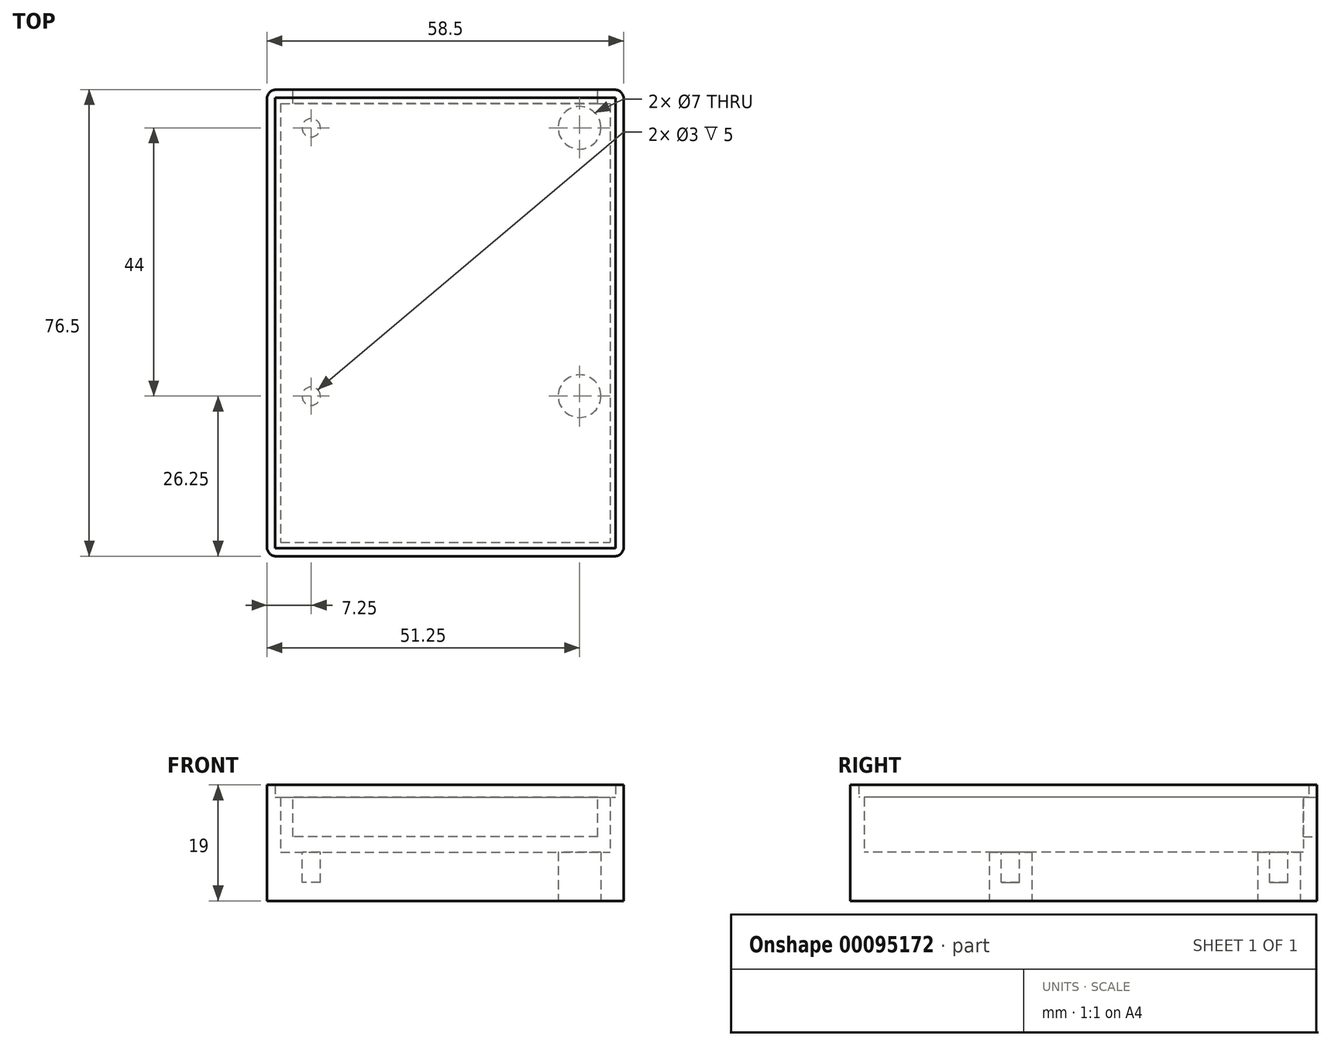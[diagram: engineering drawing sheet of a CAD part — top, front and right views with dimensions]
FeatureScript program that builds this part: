
annotation { "Feature Type Name" : "Feature", "Feature Type Description" : "" }
export const myFeature = defineFeature(function(context is Context, id is Id, definition is map)
    precondition{}
    {
        {
            var Q0;
            Q0=qCreatedBy(makeId("Top.planeOp"),FACE);
            var sketch = newSketch(context, id + "F0", { "sketchPlane" : qUnion([Q0])});
            skLineSegment(sketch, "E0.bottom", {"start": v(-25, 34) * mm, "end": v(25, 34) * mm, "construction": true});
            skLineSegment(sketch, "E0.top", {"start": v(-25, -34) * mm, "end": v(25, -34) * mm, "construction": true});
            skLineSegment(sketch, "E0.left", {"start": v(-25, 34) * mm, "end": v(-25, -34) * mm, "construction": true});
            skLineSegment(sketch, "E0.right", {"start": v(25, 34) * mm, "end": v(25, -34) * mm, "construction": true});
            skPoint(sketch, "E0.middle", {"position": v(0, 0) * mm});
            skCircle(sketch, "E1", {"center": v(-22, 32) * mm, "radius": 0.75 * mm, "construction": true});
            skCircle(sketch, "E2", {"center": v(-22, -12) * mm, "radius": 0.75 * mm, "construction": true});
            skLineSegment(sketch, "E3", {"start": v(0, 34) * mm, "end": v(0, -34) * mm, "construction": true});
            skCircle(sketch, "E4.MirrorC", {"center": v(22, 32) * mm, "radius": 0.75 * mm, "construction": true});
            skCircle(sketch, "E5.MirrorC", {"center": v(22, -12) * mm, "radius": 0.75 * mm, "construction": true});
            skLineSegment(sketch, "E6.0", {"start": v(-27, 36) * mm, "end": v(-27, -36) * mm});
            skLineSegment(sketch, "E6.1", {"start": v(-27, 36) * mm, "end": v(27, 36) * mm});
            skLineSegment(sketch, "E6.2", {"start": v(27, 36) * mm, "end": v(27, -36) * mm});
            skLineSegment(sketch, "E6.3", {"start": v(-27, -36) * mm, "end": v(27, -36) * mm});
            skLineSegment(sketch, "E7.0", {"start": v(-29.25, 38.25) * mm, "end": v(-29.25, -38.25) * mm});
            skLineSegment(sketch, "E7.1", {"start": v(-29.25, 38.25) * mm, "end": v(29.25, 38.25) * mm});
            skLineSegment(sketch, "E7.2", {"start": v(29.25, 38.25) * mm, "end": v(29.25, -38.25) * mm});
            skLineSegment(sketch, "E7.3", {"start": v(-29.25, -38.25) * mm, "end": v(29.25, -38.25) * mm});
            skCircle(sketch, "E8", {"center": v(-22, 32) * mm, "radius": 3.5 * mm});
            skCircle(sketch, "E9", {"center": v(-22, -12) * mm, "radius": 3.5 * mm});
            skCircle(sketch, "E10.MirrorC", {"center": v(22, 32) * mm, "radius": 3.5 * mm});
            skCircle(sketch, "E11.MirrorC", {"center": v(22, -12) * mm, "radius": 3.5 * mm});
            skSolve(sketch);
        }
        {
            var Q0;
            Q0=qSketchRegion(id+"F0",true);
            var Q1;
            Q1=makeQuery(id+"F0.imprint","IMPRINT",FACE,{"disambiguationData":[TD([[makeQuery(id+"F0.imprint","IMPRINT",EDGE,{"derivedFrom":sQuery(id+"F0.wireOp",EDGE,"E6.0")}),1.0]])]});
            var Q2;
            Q2=makeQuery(id+"F0.imprint","IMPRINT",FACE,{"disambiguationData":[TD([[makeQuery(id+"F0.imprint","IMPRINT",EDGE,{"derivedFrom":sQuery(id+"F0.wireOp",EDGE,"E8")}),1.0]])]});
            var Q3;
            Q3=makeQuery(id+"F0.imprint","IMPRINT",FACE,{"disambiguationData":[TD([[makeQuery(id+"F0.imprint","IMPRINT",EDGE,{"derivedFrom":sQuery(id+"F0.wireOp",EDGE,"E10.MirrorC")}),-1.0]])]});
            var Q4;
            Q4=makeQuery(id+"F0.imprint","IMPRINT",FACE,{"disambiguationData":[TD([[makeQuery(id+"F0.imprint","IMPRINT",EDGE,{"derivedFrom":sQuery(id+"F0.wireOp",EDGE,"E11.MirrorC")}),-1.0]])]});
            var Q5;
            Q5=makeQuery(id+"F0.imprint","IMPRINT",FACE,{"disambiguationData":[TD([[makeQuery(id+"F0.imprint","IMPRINT",EDGE,{"derivedFrom":sQuery(id+"F0.wireOp",EDGE,"E9")}),1.0]])]});
            extrude(context, id + "F1", {"entities" : qUnion([Q0, Q1, Q2, Q3, Q4, Q5]), "depth" : 1 * mm});
        }
        {
            var Q0;
            Q0=makeQuery(id+"F0.imprint","IMPRINT",FACE,{"disambiguationData":[TD([[makeQuery(id+"F0.imprint","IMPRINT",EDGE,{"derivedFrom":sQuery(id+"F0.wireOp",EDGE,"E6.0")}),-1.0]])]});
            extrude(context, id + "F2", {"entities" : qUnion([Q0]), "operationType" : NewBodyOperationType.ADD, "depth" : 19 * mm});
        }
        {
            var Q0;
            Q0=makeQuery(id+"F0.imprint","IMPRINT",FACE,{"disambiguationData":[TD([[makeQuery(id+"F0.imprint","IMPRINT",EDGE,{"derivedFrom":sQuery(id+"F0.wireOp",EDGE,"E9")}),1.0]])]});
            var Q1;
            Q1=makeQuery(id+"F0.imprint","IMPRINT",FACE,{"disambiguationData":[TD([[makeQuery(id+"F0.imprint","IMPRINT",EDGE,{"derivedFrom":sQuery(id+"F0.wireOp",EDGE,"E11.MirrorC")}),-1.0]])]});
            var Q2;
            Q2=makeQuery(id+"F0.imprint","IMPRINT",FACE,{"disambiguationData":[TD([[makeQuery(id+"F0.imprint","IMPRINT",EDGE,{"derivedFrom":sQuery(id+"F0.wireOp",EDGE,"E8")}),1.0]])]});
            var Q3;
            Q3=makeQuery(id+"F0.imprint","IMPRINT",FACE,{"disambiguationData":[TD([[makeQuery(id+"F0.imprint","IMPRINT",EDGE,{"derivedFrom":sQuery(id+"F0.wireOp",EDGE,"E10.MirrorC")}),-1.0]])]});
            extrude(context, id + "F3", {"entities" : qUnion([Q0, Q1, Q2, Q3]), "operationType" : NewBodyOperationType.ADD, "depth" : 8 * mm});
        }
        {
            var Q0;
            Q0=makeQuery(id+"F3.opExtrude","CAP_FACE",FACE,{"disambiguationData":[OSD([sQuery(id+"F0.wireOp",EDGE,"E11.MirrorC")])],"isStart":false});
            var sketch = newSketch(context, id + "F4", { "sketchPlane" : qUnion([Q0])});
            skCircle(sketch, "E12", {"center": v(22, -12) * mm, "radius": 1.5 * mm});
            skCircle(sketch, "E13", {"center": v(22, 32) * mm, "radius": 1.5 * mm});
            skLineSegment(sketch, "E14", {"start": v(0, -31.84) * mm, "end": v(0, 27.8) * mm, "construction": true});
            skCircle(sketch, "E15.MirrorC", {"center": v(-22, -12) * mm, "radius": 1.5 * mm});
            skCircle(sketch, "E16.MirrorC", {"center": v(-22, 32) * mm, "radius": 1.5 * mm});
            skSolve(sketch);
        }
        {
            var Q0;
            Q0=qSketchRegion(id+"F4",true);
            extrude(context, id + "F5", {"entities" : qUnion([Q0]), "operationType" : NewBodyOperationType.REMOVE, "oppositeDirection" : true, "depth" : 5 * mm});
        }
        {
            var Q0;
            Q0=makeQuery(id+"F2.opExtrude","CAP_FACE",FACE,{"disambiguationData":[OSD([sQuery(id+"F0.wireOp",EDGE,"E6.0"),sQuery(id+"F0.wireOp",EDGE,"E6.1"),sQuery(id+"F0.wireOp",EDGE,"E6.2"),sQuery(id+"F0.wireOp",EDGE,"E6.3"),sQuery(id+"F0.wireOp",EDGE,"E7.0"),sQuery(id+"F0.wireOp",EDGE,"E7.1"),sQuery(id+"F0.wireOp",EDGE,"E7.2"),sQuery(id+"F0.wireOp",EDGE,"E7.3")])],"isStart":false});
            var sketch = newSketch(context, id + "F6", { "sketchPlane" : qUnion([Q0])});
            skLineSegment(sketch, "E17.0", {"start": v(27.9, 36.9) * mm, "end": v(27.9, -36.9) * mm});
            skLineSegment(sketch, "E17.1", {"start": v(-27.9, 36.9) * mm, "end": v(27.9, 36.9) * mm});
            skLineSegment(sketch, "E17.2", {"start": v(-27.9, 36.9) * mm, "end": v(-27.9, -36.9) * mm});
            skLineSegment(sketch, "E17.3", {"start": v(-27.9, -36.9) * mm, "end": v(27.9, -36.9) * mm});
            skSolve(sketch);
        }
        {
            var Q0;
            Q0=qSketchRegion(id+"F6",true);
            extrude(context, id + "F7", {"entities" : qUnion([Q0]), "operationType" : NewBodyOperationType.REMOVE, "oppositeDirection" : true, "depth" : 2 * mm});
        }
        {
            var Q0;
            {var subQ0=sQuery(id+"F0.wireOp",EDGE,"E7.1");Q0=makeQuery(id+"F2.boolean.opBoolean","MERGE",FACE,{"derivedFrom":[makeQuery(id+"F1.opExtrude","SWEPT_FACE",FACE,{"disambiguationData":[OSD([subQ0])]}),makeQuery(id+"F2.opExtrude","SWEPT_FACE",FACE,{"disambiguationData":[OSD([subQ0])]})]});}
            var sketch = newSketch(context, id + "F8", { "sketchPlane" : qUnion([Q0])});
            skLineSegment(sketch, "E18.bottom", {"start": v(-25, 10.5) * mm, "end": v(25, 10.5) * mm});
            skLineSegment(sketch, "E18.top", {"start": v(-25, 17) * mm, "end": v(25, 17) * mm});
            skLineSegment(sketch, "E18.left", {"start": v(-25, 10.5) * mm, "end": v(-25, 17) * mm});
            skLineSegment(sketch, "E18.right", {"start": v(25, 10.5) * mm, "end": v(25, 17) * mm});
            skPoint(sketch, "E18.middle", {"position": v(0, 13.75) * mm});
            skSolve(sketch);
        }
        {
            var Q0;
            Q0=makeQuery(id+"F8.imprint","IMPRINT",FACE,{"disambiguationData":[TD([[makeQuery(id+"F8.imprint","IMPRINT",EDGE,{"derivedFrom":sQuery(id+"F8.wireOp",EDGE,"E18.bottom")}),1.0]])]});
            extrude(context, id + "F9", {"entities" : qUnion([Q0]), "operationType" : NewBodyOperationType.REMOVE, "oppositeDirection" : true, "depth" : 3 * mm});
        }
        {
            var Q0;
            {var subQ0=sQuery(id+"F0.wireOp",EDGE,"E7.3");var subQ1=sQuery(id+"F0.wireOp",EDGE,"E7.2");Q0=makeQuery(id+"F2.boolean.opBoolean","MERGE",EDGE,{"derivedFrom":[makeQuery(id+"F1.opExtrude","SWEPT_EDGE",EDGE,{"disambiguationData":[OSD([subQ1,subQ0])]}),makeQuery(id+"F2.opExtrude","SWEPT_EDGE",EDGE,{"disambiguationData":[OSD([subQ1,subQ0])]})]});}
            var Q1;
            {var subQ0=sQuery(id+"F0.wireOp",EDGE,"E7.3");var subQ1=sQuery(id+"F0.wireOp",EDGE,"E7.0");Q1=makeQuery(id+"F2.boolean.opBoolean","MERGE",EDGE,{"derivedFrom":[makeQuery(id+"F1.opExtrude","SWEPT_EDGE",EDGE,{"disambiguationData":[OSD([subQ1,subQ0])]}),makeQuery(id+"F2.opExtrude","SWEPT_EDGE",EDGE,{"disambiguationData":[OSD([subQ1,subQ0])]})]});}
            var Q2;
            {var subQ0=sQuery(id+"F0.wireOp",EDGE,"E7.1");var subQ1=sQuery(id+"F0.wireOp",EDGE,"E7.0");Q2=makeQuery(id+"F2.boolean.opBoolean","MERGE",EDGE,{"derivedFrom":[makeQuery(id+"F1.opExtrude","SWEPT_EDGE",EDGE,{"disambiguationData":[OSD([subQ1,subQ0])]}),makeQuery(id+"F2.opExtrude","SWEPT_EDGE",EDGE,{"disambiguationData":[OSD([subQ1,subQ0])]})]});}
            var Q3;
            {var subQ0=sQuery(id+"F0.wireOp",EDGE,"E7.2");var subQ1=sQuery(id+"F0.wireOp",EDGE,"E7.1");Q3=makeQuery(id+"F2.boolean.opBoolean","MERGE",EDGE,{"derivedFrom":[makeQuery(id+"F1.opExtrude","SWEPT_EDGE",EDGE,{"disambiguationData":[OSD([subQ1,subQ0])]}),makeQuery(id+"F2.opExtrude","SWEPT_EDGE",EDGE,{"disambiguationData":[OSD([subQ1,subQ0])]})]});}
            fillet(context, id + "F10", {"entities" : qUnion([Q0, Q1, Q2, Q3]), "radius" : 1.5 * mm, "tangentPropagation" : true, "allowEdgeOverflow" : false});
        }
        {
            var Q0;
            Q0=makeQuery(id+"F7.boolean.opBoolean","COPY",FACE,{"derivedFrom":makeQuery(id+"F7.opExtrude","CAP_FACE",FACE,{"disambiguationData":[OSD([sQuery(id+"F6.wireOp",EDGE,"E17.0"),sQuery(id+"F6.wireOp",EDGE,"E17.1"),sQuery(id+"F6.wireOp",EDGE,"E17.2"),sQuery(id+"F6.wireOp",EDGE,"E17.3")])],"isStart":false})});
            var sketch = newSketch(context, id + "F11", { "sketchPlane" : qUnion([Q0])});
            skLineSegment(sketch, "E19.bottom", {"start": v(-27.9, 36.9) * mm, "end": v(27.9, 36.9) * mm});
            skLineSegment(sketch, "E19.top", {"start": v(-27.9, -36.9) * mm, "end": v(27.9, -36.9) * mm});
            skLineSegment(sketch, "E19.left", {"start": v(-27.9, 36.9) * mm, "end": v(-27.9, -36.9) * mm});
            skLineSegment(sketch, "E19.right", {"start": v(27.9, 36.9) * mm, "end": v(27.9, -36.9) * mm});
            skSolve(sketch);
        }
        {
            var Q0;
            Q0 = qSketchRegion(id + "F11", true);
            extrude(context, id + "F12", {"entities" : qUnion([Q0]), "depth" : 2 * mm});
        }
    });
